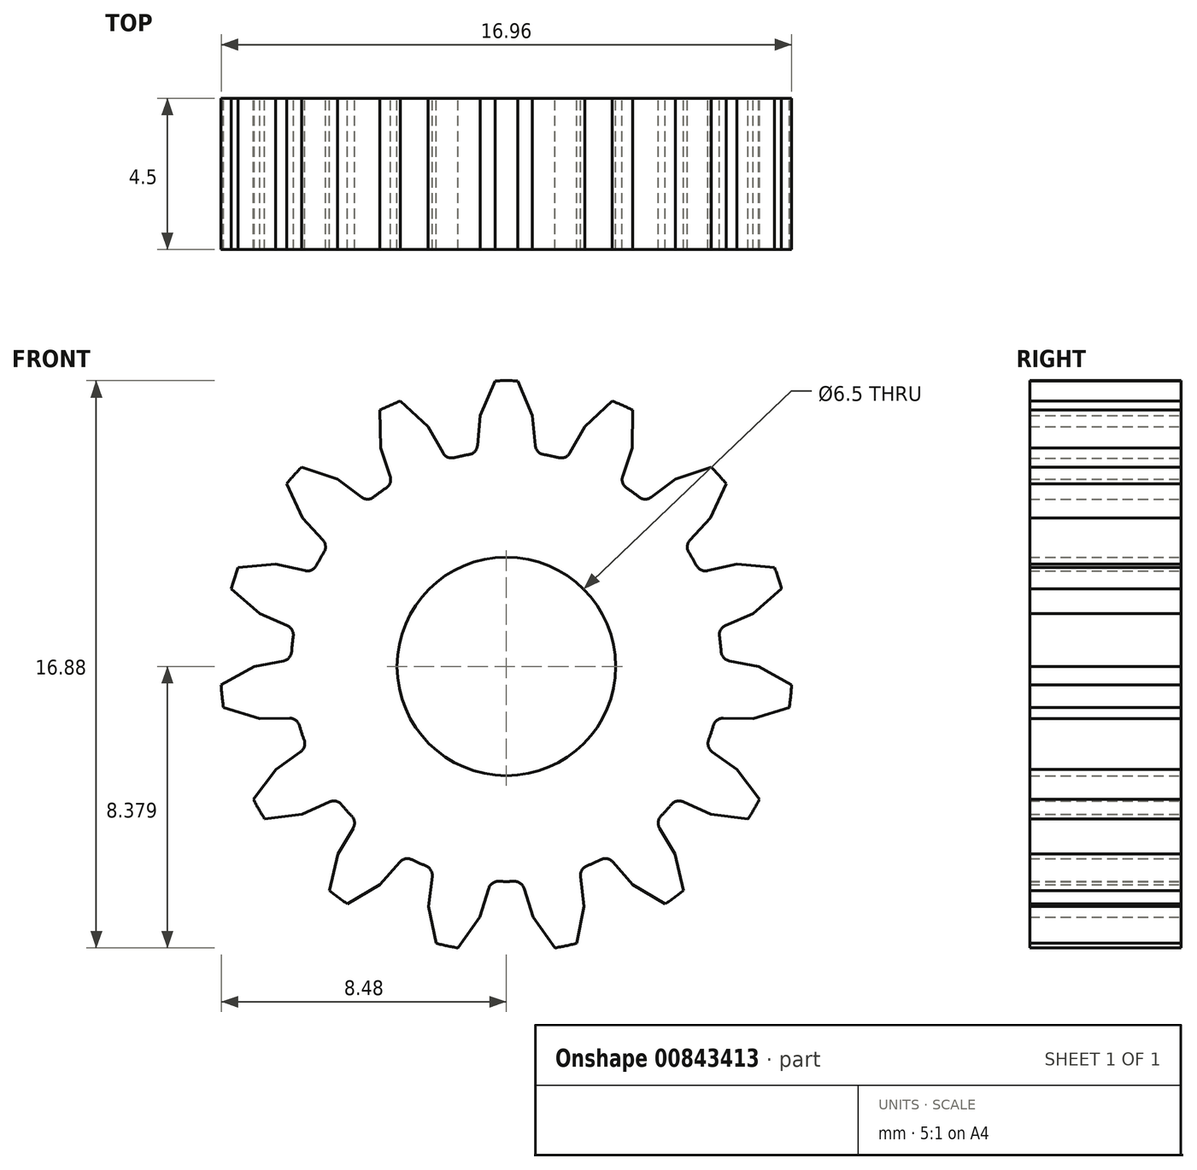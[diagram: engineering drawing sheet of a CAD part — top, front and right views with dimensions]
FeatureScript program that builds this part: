
annotation { "Feature Type Name" : "Feature", "Feature Type Description" : "" }
export const myFeature = defineFeature(function(context is Context, id is Id, definition is map)
    precondition{}
    {
        {
            var Q0;
            Q0=qCreatedBy(makeId("Front.planeOp"),FACE);
            var sketch = newSketch(context, id + "F0", { "sketchPlane" : qUnion([Q0])});
            skLineSegment(sketch, "E0", {"start": v(-6.63, 0.1) * mm, "end": v(-7.5, -0.07) * mm});
            skLineSegment(sketch, "E1", {"start": v(-7.5, -0.07) * mm, "end": v(-8.48, -0.62) * mm});
            skArc(sketch, "E2", {"start": v(-8.48, -0.62) * mm, "mid": v(-8.45, -0.95) * mm, "end": v(-8.41, -1.28) * mm});
            skLineSegment(sketch, "E3", {"start": v(-8.41, -1.28) * mm, "end": v(-7.34, -1.61) * mm});
            skLineSegment(sketch, "E4", {"start": v(-7.34, -1.61) * mm, "end": v(-6.45, -1.6) * mm});
            skArc(sketch, "E5", {"start": v(-6.15, -1.82) * mm, "mid": v(-6.26, -1.66) * mm, "end": v(-6.45, -1.6) * mm});
            skArc(sketch, "E6", {"start": v(-6.15, -1.82) * mm, "mid": v(-6.09, -2.04) * mm, "end": v(-6.01, -2.26) * mm});
            skArc(sketch, "E7", {"start": v(-6.12, -2.6) * mm, "mid": v(-6, -2.45) * mm, "end": v(-6.01, -2.26) * mm});
            skLineSegment(sketch, "E8", {"start": v(-6.12, -2.6) * mm, "end": v(-6.85, -3.12) * mm});
            skLineSegment(sketch, "E9", {"start": v(-6.85, -3.12) * mm, "end": v(-7.52, -4.02) * mm});
            skArc(sketch, "E10", {"start": v(-7.52, -4.02) * mm, "mid": v(-7.36, -4.31) * mm, "end": v(-7.19, -4.6) * mm});
            skLineSegment(sketch, "E11", {"start": v(-7.19, -4.6) * mm, "end": v(-6.07, -4.46) * mm});
            skLineSegment(sketch, "E12", {"start": v(-6.07, -4.46) * mm, "end": v(-5.26, -4.1) * mm});
            skArc(sketch, "E13", {"start": v(-4.9, -4.17) * mm, "mid": v(-5.07, -4.07) * mm, "end": v(-5.26, -4.1) * mm});
            skArc(sketch, "E14", {"start": v(-4.9, -4.17) * mm, "mid": v(-4.76, -4.34) * mm, "end": v(-4.6, -4.51) * mm});
            skArc(sketch, "E15", {"start": v(-4.56, -4.87) * mm, "mid": v(-4.52, -4.69) * mm, "end": v(-4.6, -4.51) * mm});
            skLineSegment(sketch, "E16", {"start": v(-4.56, -4.87) * mm, "end": v(-5.01, -5.64) * mm});
            skLineSegment(sketch, "E17", {"start": v(-5.01, -5.64) * mm, "end": v(-5.26, -6.74) * mm});
            skArc(sketch, "E18", {"start": v(-5.26, -6.74) * mm, "mid": v(-5, -6.94) * mm, "end": v(-4.72, -7.13) * mm});
            skLineSegment(sketch, "E19", {"start": v(-4.72, -7.13) * mm, "end": v(-3.76, -6.55) * mm});
            skLineSegment(sketch, "E20", {"start": v(-3.76, -6.55) * mm, "end": v(-3.17, -5.88) * mm});
            skArc(sketch, "E21", {"start": v(-2.81, -5.81) * mm, "mid": v(-3, -5.79) * mm, "end": v(-3.17, -5.88) * mm});
            skArc(sketch, "E22", {"start": v(-2.81, -5.81) * mm, "mid": v(-2.6, -5.9) * mm, "end": v(-2.4, -6) * mm});
            skArc(sketch, "E23", {"start": v(-2.2, -6.31) * mm, "mid": v(-2.25, -6.12) * mm, "end": v(-2.4, -6) * mm});
            skLineSegment(sketch, "E24", {"start": v(-2.2, -6.31) * mm, "end": v(-2.3, -7.2) * mm});
            skLineSegment(sketch, "E25", {"start": v(-2.3, -7.2) * mm, "end": v(-2.1, -8.3) * mm});
            skArc(sketch, "E26", {"start": v(-2.1, -8.3) * mm, "mid": v(-1.77, -8.38) * mm, "end": v(-1.44, -8.44) * mm});
            skLineSegment(sketch, "E27", {"start": v(-1.44, -8.44) * mm, "end": v(-0.8, -7.52) * mm});
            skLineSegment(sketch, "E28", {"start": v(-0.8, -7.52) * mm, "end": v(-0.53, -6.67) * mm});
            skArc(sketch, "E29", {"start": v(-0.23, -6.46) * mm, "mid": v(-0.41, -6.51) * mm, "end": v(-0.53, -6.67) * mm});
            skArc(sketch, "E30", {"start": v(-0.23, -6.46) * mm, "mid": v(0, -6.46) * mm, "end": v(0.23, -6.46) * mm});
            skArc(sketch, "E31", {"start": v(0.53, -6.67) * mm, "mid": v(0.41, -6.51) * mm, "end": v(0.23, -6.46) * mm});
            skLineSegment(sketch, "E32", {"start": v(0.53, -6.67) * mm, "end": v(0.8, -7.52) * mm});
            skLineSegment(sketch, "E33", {"start": v(0.8, -7.52) * mm, "end": v(1.44, -8.44) * mm});
            skArc(sketch, "E34", {"start": v(1.44, -8.44) * mm, "mid": v(1.77, -8.38) * mm, "end": v(2.1, -8.3) * mm});
            skLineSegment(sketch, "E35", {"start": v(2.1, -8.3) * mm, "end": v(2.3, -7.2) * mm});
            skLineSegment(sketch, "E36", {"start": v(2.3, -7.2) * mm, "end": v(2.2, -6.31) * mm});
            skArc(sketch, "E37", {"start": v(2.4, -6) * mm, "mid": v(2.25, -6.12) * mm, "end": v(2.2, -6.31) * mm});
            skArc(sketch, "E38", {"start": v(2.4, -6) * mm, "mid": v(2.6, -5.9) * mm, "end": v(2.81, -5.81) * mm});
            skArc(sketch, "E39", {"start": v(3.17, -5.88) * mm, "mid": v(3, -5.79) * mm, "end": v(2.81, -5.81) * mm});
            skLineSegment(sketch, "E40", {"start": v(3.17, -5.88) * mm, "end": v(3.76, -6.55) * mm});
            skLineSegment(sketch, "E41", {"start": v(3.76, -6.55) * mm, "end": v(4.72, -7.13) * mm});
            skArc(sketch, "E42", {"start": v(4.72, -7.13) * mm, "mid": v(5, -6.94) * mm, "end": v(5.26, -6.74) * mm});
            skLineSegment(sketch, "E43", {"start": v(5.26, -6.74) * mm, "end": v(5.01, -5.64) * mm});
            skLineSegment(sketch, "E44", {"start": v(5.01, -5.64) * mm, "end": v(4.56, -4.87) * mm});
            skArc(sketch, "E45", {"start": v(4.6, -4.51) * mm, "mid": v(4.52, -4.69) * mm, "end": v(4.56, -4.87) * mm});
            skArc(sketch, "E46", {"start": v(4.6, -4.51) * mm, "mid": v(4.76, -4.34) * mm, "end": v(4.9, -4.17) * mm});
            skArc(sketch, "E47", {"start": v(5.26, -4.1) * mm, "mid": v(5.07, -4.07) * mm, "end": v(4.9, -4.17) * mm});
            skLineSegment(sketch, "E48", {"start": v(5.26, -4.1) * mm, "end": v(6.07, -4.46) * mm});
            skLineSegment(sketch, "E49", {"start": v(6.07, -4.46) * mm, "end": v(7.19, -4.6) * mm});
            skArc(sketch, "E50", {"start": v(7.19, -4.6) * mm, "mid": v(7.36, -4.31) * mm, "end": v(7.52, -4.02) * mm});
            skLineSegment(sketch, "E51", {"start": v(7.52, -4.02) * mm, "end": v(6.85, -3.12) * mm});
            skLineSegment(sketch, "E52", {"start": v(6.85, -3.12) * mm, "end": v(6.12, -2.6) * mm});
            skArc(sketch, "E53", {"start": v(6.01, -2.26) * mm, "mid": v(6, -2.45) * mm, "end": v(6.12, -2.6) * mm});
            skArc(sketch, "E54", {"start": v(6.01, -2.26) * mm, "mid": v(6.09, -2.04) * mm, "end": v(6.15, -1.82) * mm});
            skArc(sketch, "E55", {"start": v(6.45, -1.6) * mm, "mid": v(6.26, -1.66) * mm, "end": v(6.15, -1.82) * mm});
            skLineSegment(sketch, "E56", {"start": v(6.45, -1.6) * mm, "end": v(7.34, -1.61) * mm});
            skLineSegment(sketch, "E57", {"start": v(7.34, -1.61) * mm, "end": v(8.41, -1.28) * mm});
            skArc(sketch, "E58", {"start": v(8.41, -1.28) * mm, "mid": v(8.45, -0.95) * mm, "end": v(8.48, -0.62) * mm});
            skLineSegment(sketch, "E59", {"start": v(8.48, -0.62) * mm, "end": v(7.5, -0.07) * mm});
            skLineSegment(sketch, "E60", {"start": v(7.5, -0.07) * mm, "end": v(6.63, 0.1) * mm});
            skArc(sketch, "E61", {"start": v(6.38, 0.38) * mm, "mid": v(6.46, 0.2) * mm, "end": v(6.63, 0.1) * mm});
            skArc(sketch, "E62", {"start": v(6.38, 0.38) * mm, "mid": v(6.36, 0.6) * mm, "end": v(6.34, 0.84) * mm});
            skArc(sketch, "E63", {"start": v(6.51, 1.15) * mm, "mid": v(6.37, 1.02) * mm, "end": v(6.34, 0.84) * mm});
            skLineSegment(sketch, "E64", {"start": v(6.51, 1.15) * mm, "end": v(7.33, 1.5) * mm});
            skLineSegment(sketch, "E65", {"start": v(7.33, 1.5) * mm, "end": v(8.18, 2.25) * mm});
            skArc(sketch, "E66", {"start": v(8.18, 2.25) * mm, "mid": v(8.08, 2.57) * mm, "end": v(7.97, 2.88) * mm});
            skLineSegment(sketch, "E67", {"start": v(7.97, 2.88) * mm, "end": v(6.86, 2.98) * mm});
            skLineSegment(sketch, "E68", {"start": v(6.86, 2.98) * mm, "end": v(5.98, 2.79) * mm});
            skArc(sketch, "E69", {"start": v(5.65, 2.94) * mm, "mid": v(5.8, 2.8) * mm, "end": v(5.98, 2.79) * mm});
            skArc(sketch, "E70", {"start": v(5.65, 2.94) * mm, "mid": v(5.54, 3.14) * mm, "end": v(5.42, 3.34) * mm});
            skArc(sketch, "E71", {"start": v(5.46, 3.7) * mm, "mid": v(5.38, 3.52) * mm, "end": v(5.42, 3.34) * mm});
            skLineSegment(sketch, "E72", {"start": v(5.46, 3.7) * mm, "end": v(6.06, 4.35) * mm});
            skLineSegment(sketch, "E73", {"start": v(6.06, 4.35) * mm, "end": v(6.54, 5.37) * mm});
            skArc(sketch, "E74", {"start": v(6.54, 5.37) * mm, "mid": v(6.32, 5.63) * mm, "end": v(6.09, 5.87) * mm});
            skLineSegment(sketch, "E75", {"start": v(6.09, 5.87) * mm, "end": v(5.03, 5.5) * mm});
            skLineSegment(sketch, "E76", {"start": v(5.03, 5.5) * mm, "end": v(4.3, 4.97) * mm});
            skArc(sketch, "E77", {"start": v(3.95, 4.98) * mm, "mid": v(4.13, 4.91) * mm, "end": v(4.3, 4.97) * mm});
            skArc(sketch, "E78", {"start": v(3.95, 4.98) * mm, "mid": v(3.76, 5.12) * mm, "end": v(3.57, 5.25) * mm});
            skArc(sketch, "E79", {"start": v(3.46, 5.6) * mm, "mid": v(3.46, 5.4) * mm, "end": v(3.57, 5.25) * mm});
            skLineSegment(sketch, "E80", {"start": v(3.46, 5.6) * mm, "end": v(3.74, 6.44) * mm});
            skLineSegment(sketch, "E81", {"start": v(3.74, 6.44) * mm, "end": v(3.76, 7.56) * mm});
            skArc(sketch, "E82", {"start": v(3.76, 7.56) * mm, "mid": v(3.46, 7.7) * mm, "end": v(3.15, 7.83) * mm});
            skLineSegment(sketch, "E83", {"start": v(3.15, 7.83) * mm, "end": v(2.33, 7.07) * mm});
            skLineSegment(sketch, "E84", {"start": v(2.33, 7.07) * mm, "end": v(1.89, 6.3) * mm});
            skArc(sketch, "E85", {"start": v(1.55, 6.15) * mm, "mid": v(1.75, 6.16) * mm, "end": v(1.89, 6.3) * mm});
            skArc(sketch, "E86", {"start": v(1.55, 6.15) * mm, "mid": v(1.33, 6.2) * mm, "end": v(1.1, 6.24) * mm});
            skArc(sketch, "E87", {"start": v(0.86, 6.5) * mm, "mid": v(0.94, 6.33) * mm, "end": v(1.1, 6.24) * mm});
            skLineSegment(sketch, "E88", {"start": v(0.86, 6.5) * mm, "end": v(0.78, 7.4) * mm});
            skLineSegment(sketch, "E89", {"start": v(0.78, 7.4) * mm, "end": v(0.33, 8.43) * mm});
            skArc(sketch, "E90", {"start": v(0.33, 8.43) * mm, "mid": v(0, 8.44) * mm, "end": v(-0.33, 8.43) * mm});
            skLineSegment(sketch, "E91", {"start": v(-0.33, 8.43) * mm, "end": v(-0.78, 7.4) * mm});
            skLineSegment(sketch, "E92", {"start": v(-0.78, 7.4) * mm, "end": v(-0.86, 6.5) * mm});
            skArc(sketch, "E93", {"start": v(-1.1, 6.24) * mm, "mid": v(-0.94, 6.33) * mm, "end": v(-0.86, 6.5) * mm});
            skArc(sketch, "E94", {"start": v(-1.1, 6.24) * mm, "mid": v(-1.33, 6.2) * mm, "end": v(-1.55, 6.15) * mm});
            skArc(sketch, "E95", {"start": v(-1.89, 6.3) * mm, "mid": v(-1.75, 6.16) * mm, "end": v(-1.55, 6.15) * mm});
            skLineSegment(sketch, "E96", {"start": v(-1.89, 6.3) * mm, "end": v(-2.33, 7.07) * mm});
            skLineSegment(sketch, "E97", {"start": v(-2.33, 7.07) * mm, "end": v(-3.15, 7.83) * mm});
            skArc(sketch, "E98", {"start": v(-3.15, 7.83) * mm, "mid": v(-3.46, 7.7) * mm, "end": v(-3.76, 7.56) * mm});
            skLineSegment(sketch, "E99", {"start": v(-3.76, 7.56) * mm, "end": v(-3.74, 6.44) * mm});
            skLineSegment(sketch, "E100", {"start": v(-3.74, 6.44) * mm, "end": v(-3.46, 5.6) * mm});
            skArc(sketch, "E101", {"start": v(-3.57, 5.25) * mm, "mid": v(-3.46, 5.4) * mm, "end": v(-3.46, 5.6) * mm});
            skArc(sketch, "E102", {"start": v(-3.57, 5.25) * mm, "mid": v(-3.76, 5.12) * mm, "end": v(-3.95, 4.98) * mm});
            skArc(sketch, "E103", {"start": v(-4.3, 4.97) * mm, "mid": v(-4.13, 4.91) * mm, "end": v(-3.95, 4.98) * mm});
            skLineSegment(sketch, "E104", {"start": v(-4.3, 4.97) * mm, "end": v(-5.03, 5.5) * mm});
            skLineSegment(sketch, "E105", {"start": v(-5.03, 5.5) * mm, "end": v(-6.09, 5.87) * mm});
            skArc(sketch, "E106", {"start": v(-6.09, 5.87) * mm, "mid": v(-6.32, 5.63) * mm, "end": v(-6.54, 5.37) * mm});
            skLineSegment(sketch, "E107", {"start": v(-6.54, 5.37) * mm, "end": v(-6.06, 4.35) * mm});
            skLineSegment(sketch, "E108", {"start": v(-6.06, 4.35) * mm, "end": v(-5.46, 3.7) * mm});
            skArc(sketch, "E109", {"start": v(-5.42, 3.34) * mm, "mid": v(-5.38, 3.52) * mm, "end": v(-5.46, 3.7) * mm});
            skArc(sketch, "E110", {"start": v(-5.42, 3.34) * mm, "mid": v(-5.54, 3.14) * mm, "end": v(-5.65, 2.94) * mm});
            skArc(sketch, "E111", {"start": v(-5.98, 2.79) * mm, "mid": v(-5.8, 2.8) * mm, "end": v(-5.65, 2.94) * mm});
            skLineSegment(sketch, "E112", {"start": v(-5.98, 2.79) * mm, "end": v(-6.86, 2.98) * mm});
            skLineSegment(sketch, "E113", {"start": v(-6.86, 2.98) * mm, "end": v(-7.97, 2.88) * mm});
            skArc(sketch, "E114", {"start": v(-7.97, 2.88) * mm, "mid": v(-8.08, 2.57) * mm, "end": v(-8.18, 2.25) * mm});
            skLineSegment(sketch, "E115", {"start": v(-8.18, 2.25) * mm, "end": v(-7.33, 1.5) * mm});
            skLineSegment(sketch, "E116", {"start": v(-7.33, 1.5) * mm, "end": v(-6.51, 1.15) * mm});
            skArc(sketch, "E117", {"start": v(-6.34, 0.84) * mm, "mid": v(-6.37, 1.02) * mm, "end": v(-6.51, 1.15) * mm});
            skArc(sketch, "E118", {"start": v(-6.34, 0.84) * mm, "mid": v(-6.36, 0.6) * mm, "end": v(-6.38, 0.38) * mm});
            skArc(sketch, "E119", {"start": v(-6.63, 0.1) * mm, "mid": v(-6.46, 0.2) * mm, "end": v(-6.38, 0.38) * mm});
            skCircle(sketch, "E120", {"center": v(0, -0.06) * mm, "radius": 3.25 * mm});
            skSolve(sketch);
        }
        {
            var Q0;
            Q0 = qSketchRegion(id + "F0", true);
            extrude(context, id + "F1", {"entities" : qUnion([Q0]), "depth" : 4.5 * mm, "offsetDistance" : 25 * mm});
        }
    });
